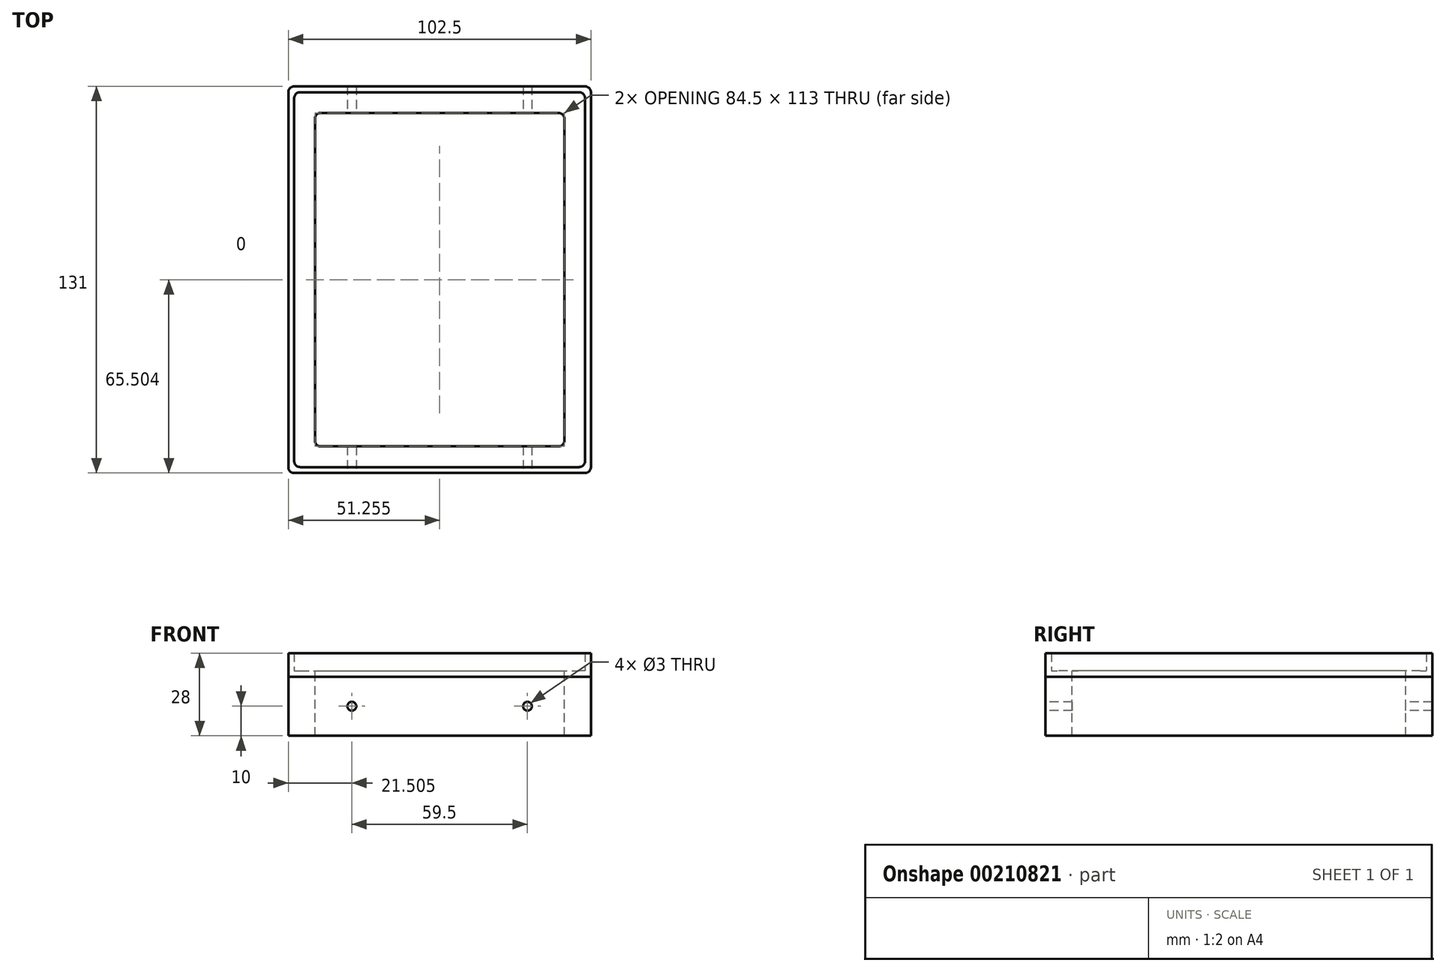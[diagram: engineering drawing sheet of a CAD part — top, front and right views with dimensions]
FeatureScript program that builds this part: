
annotation { "Feature Type Name" : "Feature", "Feature Type Description" : "" }
export const myFeature = defineFeature(function(context is Context, id is Id, definition is map)
    precondition{}
    {
        {
            var Q0;
            Q0=qCreatedBy(makeId("Top.planeOp"),FACE);
            var sketch = newSketch(context, id + "F0", { "sketchPlane" : qUnion([Q0])});
            skLineSegment(sketch, "E0.bottom", {"start": v(-48.46, 61.26) * mm, "end": v(46.04, 61.26) * mm});
            skLineSegment(sketch, "E0.top", {"start": v(-48.46, -65.74) * mm, "end": v(46.04, -65.74) * mm});
            skLineSegment(sketch, "E0.left", {"start": v(-50.46, 59.26) * mm, "end": v(-50.46, -63.74) * mm});
            skLineSegment(sketch, "E0.right", {"start": v(48.04, 59.26) * mm, "end": v(48.04, -63.74) * mm});
            skLineSegment(sketch, "E1.bottom", {"start": v(-50.46, 63.26) * mm, "end": v(48.04, 63.26) * mm});
            skLineSegment(sketch, "E1.top", {"start": v(-50.46, -67.74) * mm, "end": v(48.04, -67.74) * mm});
            skLineSegment(sketch, "E1.left", {"start": v(-52.46, 61.26) * mm, "end": v(-52.46, -65.74) * mm});
            skLineSegment(sketch, "E1.right", {"start": v(50.04, 61.26) * mm, "end": v(50.04, -65.74) * mm});
            skPoint(sketch, "E2.visualSharp", {"position": v(48.04, 61.26) * mm});
            skArc(sketch, "E2.filletArc", {"start": v(48.04, 59.26) * mm, "mid": v(47.46, 60.68) * mm, "end": v(46.04, 61.26) * mm});
            skPoint(sketch, "E3.visualSharp", {"position": v(50.04, 63.26) * mm});
            skArc(sketch, "E3.filletArc", {"start": v(50.04, 61.26) * mm, "mid": v(49.46, 62.68) * mm, "end": v(48.04, 63.26) * mm});
            skPoint(sketch, "E4.visualSharp", {"position": v(-50.46, 61.26) * mm});
            skArc(sketch, "E4.filletArc", {"start": v(-48.46, 61.26) * mm, "mid": v(-49.87, 60.68) * mm, "end": v(-50.46, 59.26) * mm});
            skPoint(sketch, "E5.visualSharp", {"position": v(-52.46, 63.26) * mm});
            skArc(sketch, "E5.filletArc", {"start": v(-50.46, 63.26) * mm, "mid": v(-51.87, 62.68) * mm, "end": v(-52.46, 61.26) * mm});
            skPoint(sketch, "E6.visualSharp", {"position": v(48.04, -65.74) * mm});
            skArc(sketch, "E6.filletArc", {"start": v(46.04, -65.74) * mm, "mid": v(47.46, -65.15) * mm, "end": v(48.04, -63.74) * mm});
            skPoint(sketch, "E7.visualSharp", {"position": v(50.04, -67.74) * mm});
            skArc(sketch, "E7.filletArc", {"start": v(48.04, -67.74) * mm, "mid": v(49.46, -67.15) * mm, "end": v(50.04, -65.74) * mm});
            skPoint(sketch, "E8.visualSharp", {"position": v(-50.46, -65.74) * mm});
            skArc(sketch, "E8.filletArc", {"start": v(-50.46, -63.74) * mm, "mid": v(-49.87, -65.15) * mm, "end": v(-48.46, -65.74) * mm});
            skPoint(sketch, "E9.visualSharp", {"position": v(-52.46, -67.74) * mm});
            skArc(sketch, "E9.filletArc", {"start": v(-52.46, -65.74) * mm, "mid": v(-51.87, -67.15) * mm, "end": v(-50.46, -67.74) * mm});
            skSolve(sketch);
        }
        {
            var Q0;
            Q0 = qSketchRegion(id + "F0", true);
            extrude(context, id + "F1", {"entities" : qUnion([Q0]), "depth" : 6 * mm});
        }
        {
            var Q0;
            Q0=qCreatedBy(makeId("Top.planeOp"),FACE);
            var sketch = newSketch(context, id + "F2", { "sketchPlane" : qUnion([Q0])});
            skLineSegment(sketch, "E10.bottom", {"start": v(-50.46, 63.26) * mm, "end": v(48.04, 63.26) * mm});
            skLineSegment(sketch, "E10.top", {"start": v(-50.46, -67.74) * mm, "end": v(48.04, -67.74) * mm});
            skLineSegment(sketch, "E10.left", {"start": v(-52.46, 61.26) * mm, "end": v(-52.46, -65.74) * mm});
            skLineSegment(sketch, "E10.right", {"start": v(50.04, 61.26) * mm, "end": v(50.04, -65.74) * mm});
            skLineSegment(sketch, "E11.bottom", {"start": v(-41.46, 54.26) * mm, "end": v(39.04, 54.26) * mm});
            skLineSegment(sketch, "E11.top", {"start": v(-41.46, -58.74) * mm, "end": v(39.04, -58.74) * mm});
            skLineSegment(sketch, "E11.left", {"start": v(-43.46, 52.26) * mm, "end": v(-43.46, -56.74) * mm});
            skLineSegment(sketch, "E11.right", {"start": v(41.04, 52.26) * mm, "end": v(41.04, -56.74) * mm});
            skPoint(sketch, "E12.visualSharp", {"position": v(-43.46, -58.74) * mm});
            skArc(sketch, "E12.filletArc", {"start": v(-43.46, -56.74) * mm, "mid": v(-42.87, -58.15) * mm, "end": v(-41.46, -58.74) * mm});
            skPoint(sketch, "E13.visualSharp", {"position": v(41.04, -58.74) * mm});
            skArc(sketch, "E13.filletArc", {"start": v(39.04, -58.74) * mm, "mid": v(40.46, -58.15) * mm, "end": v(41.04, -56.74) * mm});
            skPoint(sketch, "E14.visualSharp", {"position": v(41.04, 54.26) * mm});
            skArc(sketch, "E14.filletArc", {"start": v(41.04, 52.26) * mm, "mid": v(40.46, 53.68) * mm, "end": v(39.04, 54.26) * mm});
            skPoint(sketch, "E15.visualSharp", {"position": v(-43.46, 54.26) * mm});
            skArc(sketch, "E15.filletArc", {"start": v(-41.46, 54.26) * mm, "mid": v(-42.87, 53.68) * mm, "end": v(-43.46, 52.26) * mm});
            skPoint(sketch, "E16.visualSharp", {"position": v(-52.46, -67.74) * mm});
            skArc(sketch, "E16.filletArc", {"start": v(-52.46, -65.74) * mm, "mid": v(-51.87, -67.15) * mm, "end": v(-50.46, -67.74) * mm});
            skPoint(sketch, "E17.visualSharp", {"position": v(50.04, -67.74) * mm});
            skArc(sketch, "E17.filletArc", {"start": v(48.04, -67.74) * mm, "mid": v(49.46, -67.15) * mm, "end": v(50.04, -65.74) * mm});
            skPoint(sketch, "E18.visualSharp", {"position": v(50.04, 63.26) * mm});
            skArc(sketch, "E18.filletArc", {"start": v(50.04, 61.26) * mm, "mid": v(49.46, 62.68) * mm, "end": v(48.04, 63.26) * mm});
            skPoint(sketch, "E19.visualSharp", {"position": v(-52.46, 63.26) * mm});
            skArc(sketch, "E19.filletArc", {"start": v(-50.46, 63.26) * mm, "mid": v(-51.87, 62.68) * mm, "end": v(-52.46, 61.26) * mm});
            skSolve(sketch);
        }
        {
            var Q0;
            Q0 = qSketchRegion(id + "F2", true);
            extrude(context, id + "F3", {"entities" : qUnion([Q0]), "operationType" : NewBodyOperationType.ADD, "oppositeDirection" : true, "depth" : 2 * mm});
        }
        {
            var Q0;
            Q0=makeQuery(id+"F3.opExtrude","CAP_FACE",FACE,{"disambiguationData":[OSD([sQuery(id+"F2.wireOp",EDGE,"E10.bottom"),sQuery(id+"F2.wireOp",EDGE,"E10.top"),sQuery(id+"F2.wireOp",EDGE,"E10.left"),sQuery(id+"F2.wireOp",EDGE,"E10.right"),sQuery(id+"F2.wireOp",EDGE,"E11.bottom"),sQuery(id+"F2.wireOp",EDGE,"E11.top"),sQuery(id+"F2.wireOp",EDGE,"E11.left"),sQuery(id+"F2.wireOp",EDGE,"E11.right"),sQuery(id+"F2.wireOp",EDGE,"E12.filletArc"),sQuery(id+"F2.wireOp",EDGE,"E13.filletArc"),sQuery(id+"F2.wireOp",EDGE,"E14.filletArc"),sQuery(id+"F2.wireOp",EDGE,"E15.filletArc"),sQuery(id+"F2.wireOp",EDGE,"E16.filletArc"),sQuery(id+"F2.wireOp",EDGE,"E17.filletArc"),sQuery(id+"F2.wireOp",EDGE,"E18.filletArc"),sQuery(id+"F2.wireOp",EDGE,"E19.filletArc")])],"isStart":false});
            extrude(context, id + "F4", {"entities" : qUnion([Q0]), "depth" : 20 * mm});
        }
        {
            var Q0;
            Q0=makeQuery(id+"F4.opExtrude","SWEPT_FACE",FACE,{"disambiguationData":[OSD([sQuery(id+"F2.wireOp",EDGE,"E10.top")])]});
            var sketch = newSketch(context, id + "F5", { "sketchPlane" : qUnion([Q0])});
            skCircle(sketch, "E20", {"center": v(28.54, -12) * mm, "radius": 1.5 * mm});
            skCircle(sketch, "E21", {"center": v(-30.96, -12) * mm, "radius": 1.5 * mm});
            skSolve(sketch);
        }
        {
            var Q0;
            Q0 = qSketchRegion(id + "F5", true);
            extrude(context, id + "F6", {"entities" : qUnion([Q0]), "operationType" : NewBodyOperationType.REMOVE, "oppositeDirection" : true, "depth" : 135 * mm});
        }
    });
